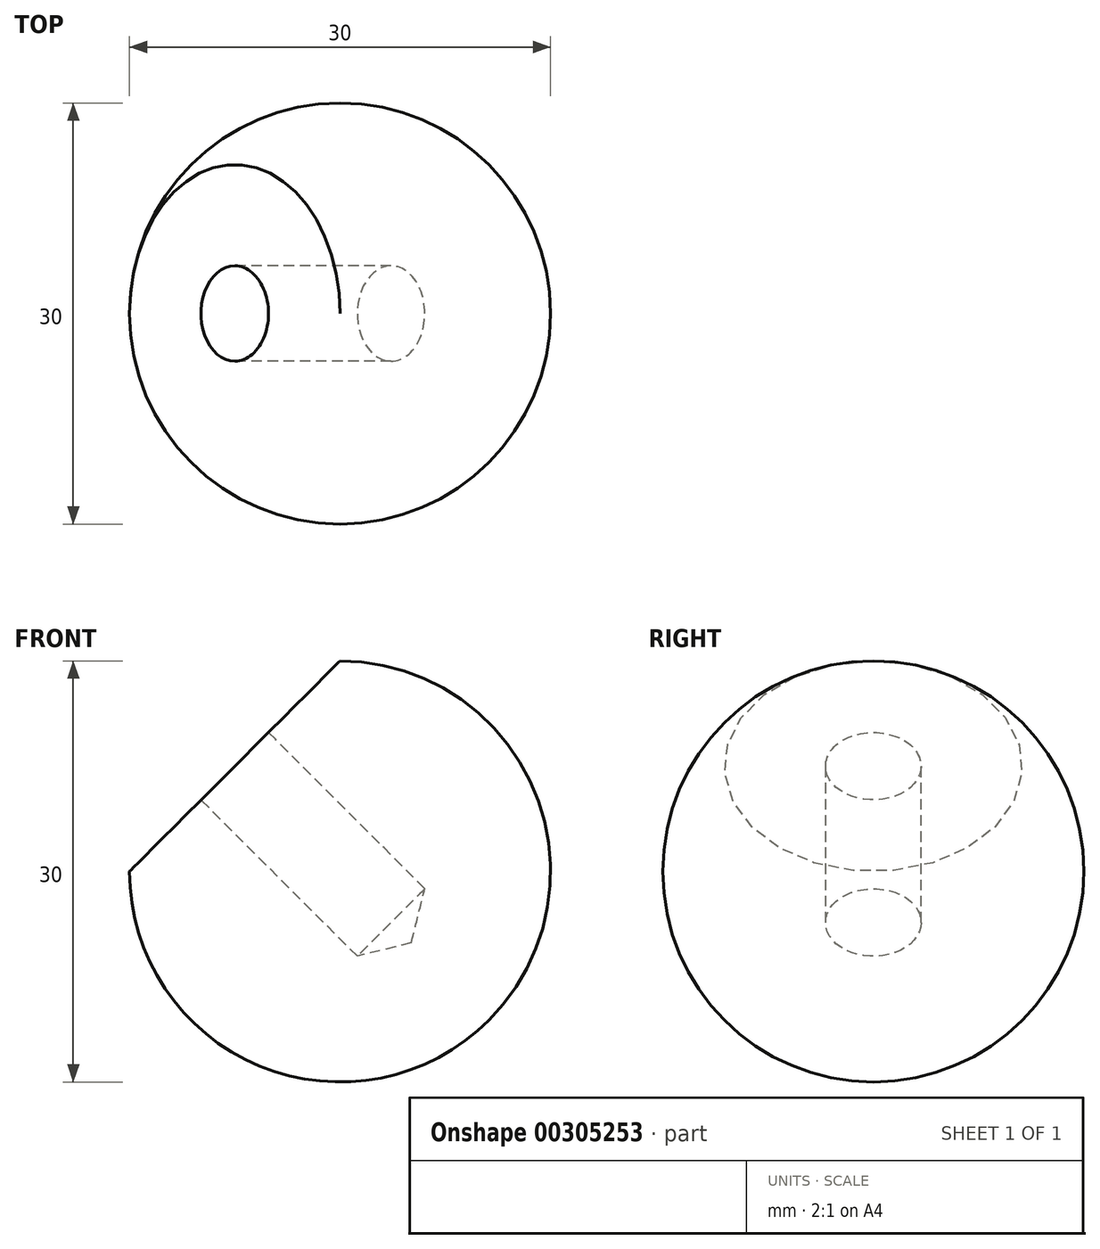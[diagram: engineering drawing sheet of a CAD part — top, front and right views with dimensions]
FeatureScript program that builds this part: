
annotation { "Feature Type Name" : "Feature", "Feature Type Description" : "" }
export const myFeature = defineFeature(function(context is Context, id is Id, definition is map)
    precondition{}
    {
        {
            var Q0;
            Q0=qCreatedBy(makeId("Front.planeOp"),FACE);
            var sketch = newSketch(context, id + "F0", { "sketchPlane" : qUnion([Q0])});
            skArc(sketch, "E0", {"start": v(-15, 0) * mm, "mid": v(10.6, -10.6) * mm, "end": v(0, 15) * mm});
            skLineSegment(sketch, "E1", {"start": v(-15, 0) * mm, "end": v(0, 15) * mm});
            skLineSegment(sketch, "E2", {"start": v(-7.5, 7.5) * mm, "end": v(10.6, -10.6) * mm});
            skSolve(sketch);
        }
        {
            var Q0;
            {var subQ3=sQuery(id+"F0.wireOp",EDGE,"E2");Q0=makeQuery(id+"F0.imprint","IMPRINT",FACE,{"disambiguationData":[TD([[makeQuery(id+"F0.imprint","IMPRINT",EDGE,{"derivedFrom":subQ3}),1.0]])]});}
            var Q1;
            Q1=sQuery(id+"F0.wireOp",EDGE,"E2");
            revolve(context, id + "F1", {"entities" : qUnion([Q0]), "axis" : qUnion([Q1]), "revolveType" : RevolveType.FULL});
        }
        {
            var Q0;
            Q0=makeQuery(id+"F1.opRevolve","SWEPT_FACE",FACE,{"disambiguationData":[OSD([sQuery(id+"F0.wireOp",EDGE,"E1")])]});
            var sketch = newSketch(context, id + "F2", { "sketchPlane" : qUnion([Q0])});
            skLineSegment(sketch, "E3", {"start": v(0, 0) * mm, "end": v(10.6, 0) * mm, "construction": true});
            skLineSegment(sketch, "E4", {"start": v(0, 0) * mm, "end": v(0, -10.6) * mm, "construction": true});
            skLineSegment(sketch, "E5", {"start": v(0, 0) * mm, "end": v(-10.6, 0) * mm, "construction": true});
            skLineSegment(sketch, "E6", {"start": v(0, 0) * mm, "end": v(0, 10.6) * mm, "construction": true});
            skSolve(sketch);
        }
        {
            var Q0;
            Q0=sQuery(id+"F2.wireOp",VERTEX,"E6.start");
            var Q1;
            Q1=makeQuery(id+"F1.opRevolve","SWEPT_BODY",BODY,{"disambiguationData":[OSD([sQuery(id+"F0.wireOp",EDGE,"E0"),sQuery(id+"F0.wireOp",EDGE,"E1"),sQuery(id+"F0.wireOp",EDGE,"E2")])]});
            hole(context, id + "F3", {"style" : HoleStyle.SIMPLE, "endStyle" : HoleEndStyle.BLIND, "standardTappedOrClearance" : lookupTablePath({ "standard" : "ISO", "engagement" : "75%", "pitch" : "1.25 mm", "size" : "M8", "type" : "Tapped" }), "standardBlindInLast" : lookupTablePath({ "standard" : "ISO", "engagement" : "75%", "pitch" : "1.25 mm", "size" : "M8", "type" : "Tapped" }), "holeDiameter" : 6.8 * mm, "showTappedDepth" : true, "holeDepth" : 15.75 * mm, "tappedDepth" : 12 * mm, "tapClearance" : 3, "locations" : qUnion([Q0]), "scope" : qUnion([Q1]), "majorDiameter" : 8 * mm});
        }
    });
